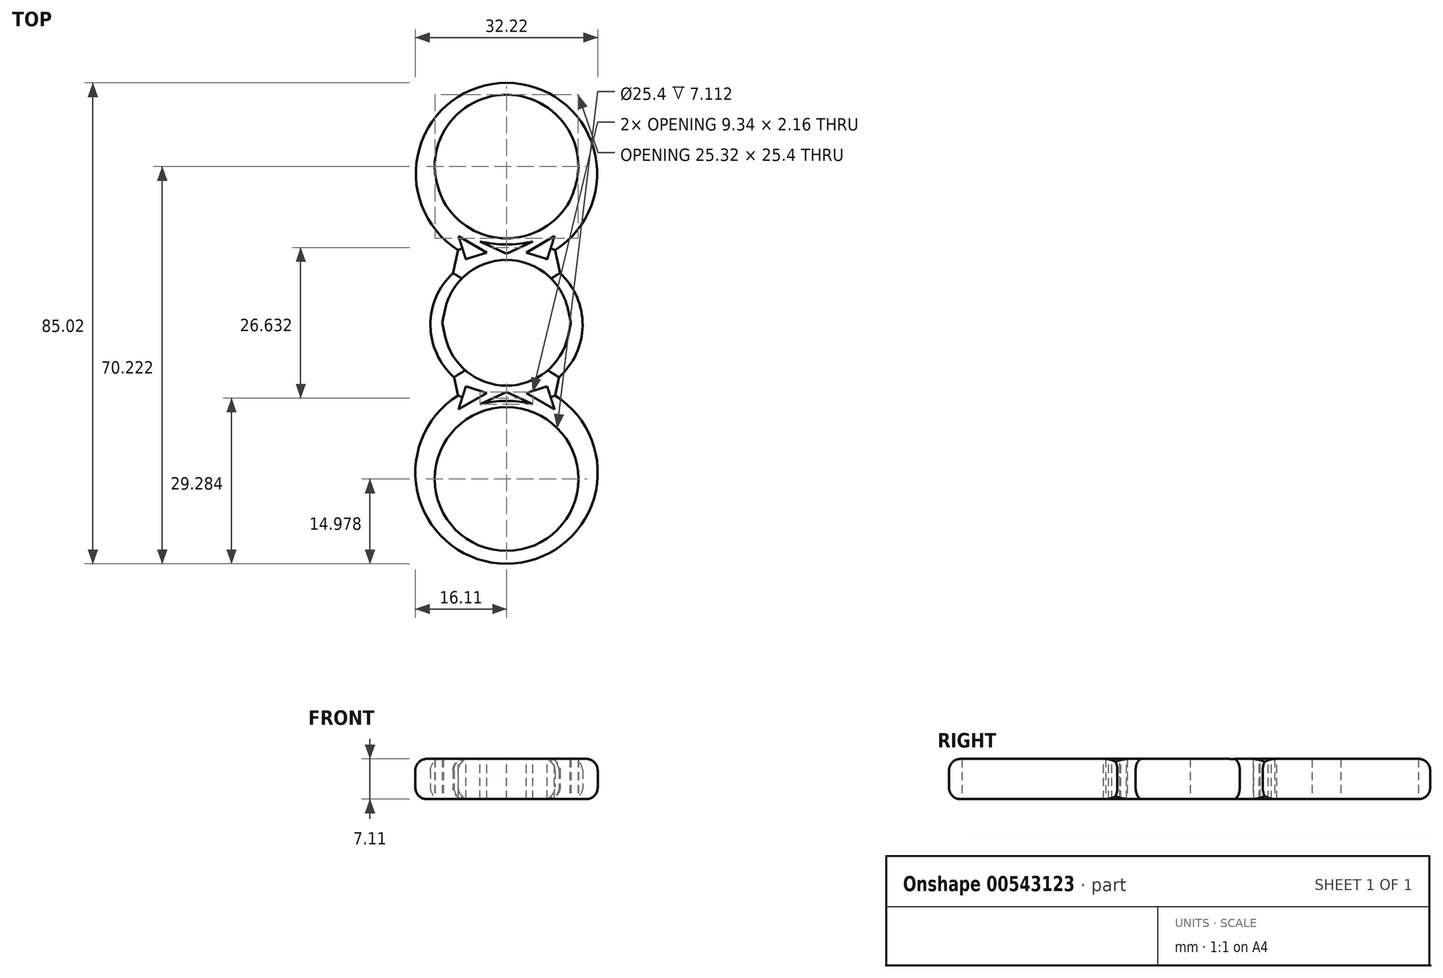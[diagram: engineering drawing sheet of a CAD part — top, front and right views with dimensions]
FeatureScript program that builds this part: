
annotation { "Feature Type Name" : "Feature", "Feature Type Description" : "" }
export const myFeature = defineFeature(function(context is Context, id is Id, definition is map)
    precondition{}
    {
        {
            var Q0;
            Q0=qCreatedBy(makeId("Top.planeOp"),FACE);
            var sketch = newSketch(context, id + "F0", { "sketchPlane" : qUnion([Q0])});
            skCircle(sketch, "E0", {"center": v(0, 0) * mm, "radius": 11.11 * mm});
            skArc(sketch, "E1", {"start": v(-11.15, 21.55) * mm, "mid": v(0, 14.92) * mm, "end": v(11.15, 21.55) * mm});
            skCircle(sketch, "E2", {"center": v(0, -27.62) * mm, "radius": 12.7 * mm});
            skLineSegment(sketch, "E3", {"start": v(-11.15, 21.55) * mm, "end": v(-8.57, 12.85) * mm});
            skLineSegment(sketch, "E4", {"start": v(-8.57, 12.85) * mm, "end": v(-9.46, 8.77) * mm});
            skLineSegment(sketch, "E5", {"start": v(-53.4, 0) * mm, "end": v(49.69, 0) * mm});
            skLineSegment(sketch, "E6", {"start": v(0, 61.11) * mm, "end": v(0, -59.4) * mm});
            skLineSegment(sketch, "E7.MirrorCS", {"start": v(-11.15, -21.55) * mm, "end": v(-8.57, -12.85) * mm});
            skLineSegment(sketch, "E8.MirrorCS", {"start": v(-8.57, -12.85) * mm, "end": v(-9.27, -9.61) * mm});
            skLineSegment(sketch, "E9.MirrorCS", {"start": v(11.15, 21.55) * mm, "end": v(8.57, 12.85) * mm});
            skLineSegment(sketch, "E10.MirrorCS", {"start": v(8.57, 12.85) * mm, "end": v(9.46, 8.77) * mm});
            skLineSegment(sketch, "E11.MirrorCS", {"start": v(8.57, -12.85) * mm, "end": v(9.27, -9.61) * mm});
            skLineSegment(sketch, "E12.MirrorCS", {"start": v(11.15, -21.55) * mm, "end": v(8.57, -12.85) * mm});
            skArc(sketch, "E13", {"start": v(8.57, 12.85) * mm, "mid": v(0, 42.42) * mm, "end": v(-8.57, 12.85) * mm});
            skArc(sketch, "E14", {"start": v(-8.57, -12.85) * mm, "mid": v(0, -42.6) * mm, "end": v(8.57, -12.85) * mm});
            skArc(sketch, "E15", {"start": v(9.27, -9.61) * mm, "mid": v(13.44, -0.46) * mm, "end": v(9.46, 8.77) * mm});
            skArc(sketch, "E16.MirrorCS", {"start": v(-9.27, -9.61) * mm, "mid": v(-13.44, -0.46) * mm, "end": v(-9.46, 8.77) * mm});
            skArc(sketch, "E17.trimOffspring", {"start": v(12.66, 26.62) * mm, "mid": v(0, 40.32) * mm, "end": v(-12.66, 26.62) * mm});
            skLineSegment(sketch, "E18.trimOffspring", {"start": v(10.86, 2.37) * mm, "end": v(11.37, 0) * mm});
            skLineSegment(sketch, "E19.trimOffspring", {"start": v(10.86, -2.37) * mm, "end": v(11.37, 0) * mm});
            skLineSegment(sketch, "E20.trimOffspring", {"start": v(-10.86, -2.37) * mm, "end": v(-11.37, 0) * mm});
            skLineSegment(sketch, "E21.trimOffspring", {"start": v(-10.86, 2.37) * mm, "end": v(-11.37, 0) * mm});
            skPoint(sketch, "E22.orphan", {"position": v(12.66, -26.62) * mm});
            skPoint(sketch, "E23.orphan", {"position": v(-12.66, -26.62) * mm});
            skArc(sketch, "E24", {"start": v(11.15, 21.55) * mm, "mid": v(12.1, 24.02) * mm, "end": v(12.66, 26.62) * mm});
            skArc(sketch, "E25", {"start": v(-12.66, 26.62) * mm, "mid": v(-12.1, 24.02) * mm, "end": v(-11.15, 21.55) * mm});
            skSolve(sketch);
        }
        {
            var Q0;
            Q0 = qSketchRegion(id + "F0", true);
            extrude(context, id + "F1", {"entities" : qUnion([Q0]), "depth" : 7.11 * mm, "offsetDistance" : 25.4 * mm});
        }
        {
            var Q0;
            Q0=makeQuery(id+"F1.opExtrude","CAP_FACE",FACE,{"disambiguationData":[OSD([sQuery(id+"F0.wireOp",EDGE,"E0"),sQuery(id+"F0.wireOp",EDGE,"E1"),sQuery(id+"F0.wireOp",EDGE,"E2"),sQuery(id+"F0.wireOp",EDGE,"E3"),sQuery(id+"F0.wireOp",EDGE,"E4"),sQuery(id+"F0.wireOp",EDGE,"E8.MirrorCS"),sQuery(id+"F0.wireOp",EDGE,"E9.MirrorCS"),sQuery(id+"F0.wireOp",EDGE,"E10.MirrorCS"),sQuery(id+"F0.wireOp",EDGE,"E11.MirrorCS"),sQuery(id+"F0.wireOp",EDGE,"E13"),sQuery(id+"F0.wireOp",EDGE,"E14"),sQuery(id+"F0.wireOp",EDGE,"E15"),sQuery(id+"F0.wireOp",EDGE,"E16.MirrorCS"),sQuery(id+"F0.wireOp",EDGE,"E17.trimOffspring"),sQuery(id+"F0.wireOp",EDGE,"E18.trimOffspring"),sQuery(id+"F0.wireOp",EDGE,"E19.trimOffspring"),sQuery(id+"F0.wireOp",EDGE,"E20.trimOffspring"),sQuery(id+"F0.wireOp",EDGE,"E21.trimOffspring")])],"isStart":false});
            var sketch = newSketch(context, id + "F2", { "sketchPlane" : qUnion([Q0])});
            skLineSegment(sketch, "E26", {"start": v(8.48, -15.3) * mm, "end": v(7.19, -11.25) * mm});
            skLineSegment(sketch, "E27", {"start": v(7.19, -11.25) * mm, "end": v(3.48, -12.43) * mm});
            skLineSegment(sketch, "E28", {"start": v(3.48, -12.43) * mm, "end": v(8.48, -15.3) * mm});
            skLineSegment(sketch, "E29.MirrorCS", {"start": v(-3.48, -12.43) * mm, "end": v(-8.48, -15.3) * mm});
            skLineSegment(sketch, "E30.MirrorCS", {"start": v(-8.48, -15.3) * mm, "end": v(-7.19, -11.25) * mm});
            skLineSegment(sketch, "E31.MirrorCS", {"start": v(-7.19, -11.25) * mm, "end": v(-3.48, -12.43) * mm});
            skLineSegment(sketch, "E32.MirrorCS", {"start": v(7.19, 11.25) * mm, "end": v(3.48, 12.43) * mm});
            skLineSegment(sketch, "E33.MirrorCS", {"start": v(8.48, 15.3) * mm, "end": v(7.19, 11.25) * mm});
            skLineSegment(sketch, "E34.MirrorCS", {"start": v(3.48, 12.43) * mm, "end": v(8.48, 15.3) * mm});
            skLineSegment(sketch, "E35.MirrorCS", {"start": v(-7.19, 11.25) * mm, "end": v(-3.48, 12.43) * mm});
            skLineSegment(sketch, "E36.MirrorCS", {"start": v(-3.48, 12.43) * mm, "end": v(-8.48, 15.3) * mm});
            skLineSegment(sketch, "E37.MirrorCS", {"start": v(-8.48, 15.3) * mm, "end": v(-7.19, 11.25) * mm});
            skLineSegment(sketch, "E38", {"start": v(-4.67, 14.4) * mm, "end": v(0, 12.24) * mm});
            skLineSegment(sketch, "E39.MirrorCS", {"start": v(4.67, 14.4) * mm, "end": v(0, 12.24) * mm});
            skArc(sketch, "E40", {"start": v(-4.67, 14.4) * mm, "mid": v(0, 13.83) * mm, "end": v(4.67, 14.4) * mm});
            skLineSegment(sketch, "E41.MirrorCS", {"start": v(-4.67, -14.4) * mm, "end": v(0, -12.24) * mm});
            skLineSegment(sketch, "E42.MirrorCS", {"start": v(4.67, -14.4) * mm, "end": v(0, -12.24) * mm});
            skArc(sketch, "E43.MirrorCS", {"start": v(-4.67, -14.4) * mm, "mid": v(0, -13.83) * mm, "end": v(4.67, -14.4) * mm});
            skSolve(sketch);
        }
        {
            var Q0;
            Q0=makeQuery(id+"F2.imprint","IMPRINT",FACE,{"disambiguationData":[TD([[makeQuery(id+"F2.imprint","IMPRINT",EDGE,{"derivedFrom":sQuery(id+"F2.wireOp",EDGE,"E26")}),1.0]])]});
            var Q1;
            Q1=makeQuery(id+"F2.imprint","IMPRINT",FACE,{"disambiguationData":[TD([[makeQuery(id+"F2.imprint","IMPRINT",EDGE,{"derivedFrom":sQuery(id+"F2.wireOp",EDGE,"E29.MirrorCS")}),-1.0]])]});
            var Q2;
            Q2=makeQuery(id+"F2.imprint","IMPRINT",FACE,{"disambiguationData":[TD([[makeQuery(id+"F2.imprint","IMPRINT",EDGE,{"derivedFrom":sQuery(id+"F2.wireOp",EDGE,"E32.MirrorCS")}),-1.0]])]});
            var Q3;
            Q3=makeQuery(id+"F2.imprint","IMPRINT",FACE,{"disambiguationData":[TD([[makeQuery(id+"F2.imprint","IMPRINT",EDGE,{"derivedFrom":sQuery(id+"F2.wireOp",EDGE,"E35.MirrorCS")}),1.0]])]});
            extrude(context, id + "F3", {"entities" : qUnion([Q0, Q1, Q2, Q3]), "operationType" : NewBodyOperationType.REMOVE, "oppositeDirection" : true, "depth" : 25.4 * mm, "offsetDistance" : 25.4 * mm});
        }
        {
            var Q0;
            Q0=makeQuery(id+"F1.opExtrude","CAP_EDGE",EDGE,{"disambiguationData":[OSD([sQuery(id+"F0.wireOp",EDGE,"E13")])],"isStart":false});
            var Q1;
            Q1=makeQuery(id+"F1.opExtrude","CAP_EDGE",EDGE,{"disambiguationData":[OSD([sQuery(id+"F0.wireOp",EDGE,"E15")])],"isStart":false});
            var Q2;
            Q2=makeQuery(id+"F1.opExtrude","CAP_EDGE",EDGE,{"disambiguationData":[OSD([sQuery(id+"F0.wireOp",EDGE,"E16.MirrorCS")])],"isStart":false});
            var Q3;
            Q3=makeQuery(id+"F1.opExtrude","CAP_EDGE",EDGE,{"disambiguationData":[OSD([sQuery(id+"F0.wireOp",EDGE,"E14")])],"isStart":false});
            var Q4;
            Q4=makeQuery(id+"F1.opExtrude","CAP_EDGE",EDGE,{"disambiguationData":[OSD([sQuery(id+"F0.wireOp",EDGE,"E15")])],"isStart":true});
            var Q5;
            Q5=makeQuery(id+"F1.opExtrude","CAP_EDGE",EDGE,{"disambiguationData":[OSD([sQuery(id+"F0.wireOp",EDGE,"E13")])],"isStart":true});
            var Q6;
            Q6=makeQuery(id+"F1.opExtrude","CAP_EDGE",EDGE,{"disambiguationData":[OSD([sQuery(id+"F0.wireOp",EDGE,"E11.MirrorCS")])],"isStart":false});
            var Q7;
            Q7=makeQuery(id+"F1.opExtrude","CAP_EDGE",EDGE,{"disambiguationData":[OSD([sQuery(id+"F0.wireOp",EDGE,"E11.MirrorCS")])],"isStart":true});
            var Q8;
            Q8=makeQuery(id+"F1.opExtrude","CAP_EDGE",EDGE,{"disambiguationData":[OSD([sQuery(id+"F0.wireOp",EDGE,"E10.MirrorCS")])],"isStart":false});
            var Q9;
            Q9=makeQuery(id+"F1.opExtrude","CAP_EDGE",EDGE,{"disambiguationData":[OSD([sQuery(id+"F0.wireOp",EDGE,"E10.MirrorCS")])],"isStart":true});
            var Q10;
            Q10=makeQuery(id+"F1.opExtrude","CAP_EDGE",EDGE,{"disambiguationData":[OSD([sQuery(id+"F0.wireOp",EDGE,"E14")])],"isStart":true});
            var Q11;
            Q11=makeQuery(id+"F1.opExtrude","CAP_EDGE",EDGE,{"disambiguationData":[OSD([sQuery(id+"F0.wireOp",EDGE,"E16.MirrorCS")])],"isStart":true});
            var Q12;
            Q12=makeQuery(id+"F1.opExtrude","CAP_EDGE",EDGE,{"disambiguationData":[OSD([sQuery(id+"F0.wireOp",EDGE,"E4")])],"isStart":true});
            var Q13;
            Q13=makeQuery(id+"F1.opExtrude","CAP_EDGE",EDGE,{"disambiguationData":[OSD([sQuery(id+"F0.wireOp",EDGE,"E4")])],"isStart":false});
            var Q14;
            Q14=makeQuery(id+"F1.opExtrude","CAP_EDGE",EDGE,{"disambiguationData":[OSD([sQuery(id+"F0.wireOp",EDGE,"E8.MirrorCS")])],"isStart":true});
            var Q15;
            Q15=makeQuery(id+"F1.opExtrude","CAP_EDGE",EDGE,{"disambiguationData":[OSD([sQuery(id+"F0.wireOp",EDGE,"E8.MirrorCS")])],"isStart":false});
            fillet(context, id + "F4", {"entities" : qUnion([Q0, Q1, Q2, Q3, Q4, Q5, Q6, Q7, Q8, Q9, Q10, Q11, Q12, Q13, Q14, Q15]), "radius" : 2.03 * mm, "tangentPropagation" : true, "allowEdgeOverflow" : false});
        }
        {
            var Q0;
            Q0 = qSketchRegion(id + "F2", true);
            extrude(context, id + "F5", {"entities" : qUnion([Q0]), "operationType" : NewBodyOperationType.REMOVE, "oppositeDirection" : true, "depth" : 25.4 * mm, "offsetDistance" : 25.4 * mm});
        }
    });
